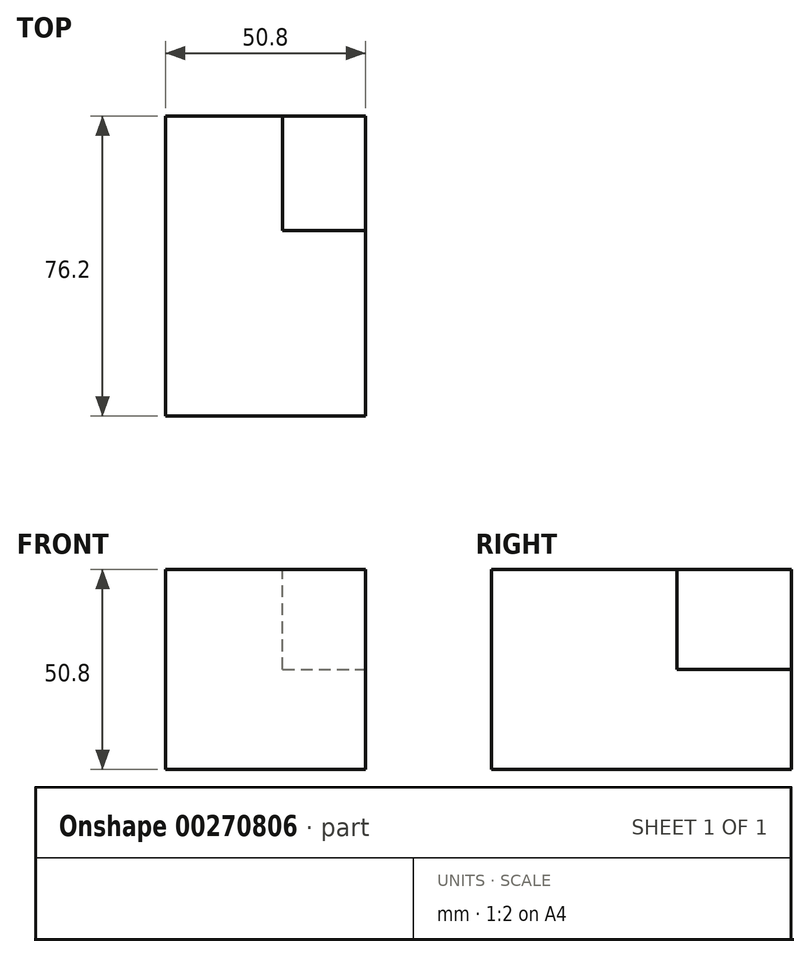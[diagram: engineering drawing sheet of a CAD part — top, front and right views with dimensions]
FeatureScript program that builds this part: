
annotation { "Feature Type Name" : "Feature", "Feature Type Description" : "" }
export const myFeature = defineFeature(function(context is Context, id is Id, definition is map)
    precondition{}
    {
        {
            var Q0;
            Q0=qCreatedBy(makeId("Front.planeOp"),FACE);
            var sketch = newSketch(context, id + "F0", { "sketchPlane" : qUnion([Q0])});
            skLineSegment(sketch, "E0", {"start": v(0, 0) * mm, "end": v(-50.8, 0) * mm});
            skLineSegment(sketch, "E1", {"start": v(-50.8, 0) * mm, "end": v(-50.8, 50.8) * mm});
            skLineSegment(sketch, "E2", {"start": v(-50.8, 50.8) * mm, "end": v(0, 50.8) * mm});
            skLineSegment(sketch, "E3", {"start": v(0, 50.8) * mm, "end": v(0, 0) * mm});
            skSolve(sketch);
        }
        {
            var Q0;
            Q0 = qSketchRegion(id + "F0", true);
            extrude(context, id + "F1", {"entities" : qUnion([Q0]), "depth" : 76.2 * mm});
        }
        {
            var Q0;
            Q0=makeQuery(id+"F1.opExtrude","SWEPT_FACE",FACE,{"disambiguationData":[OSD([sQuery(id+"F0.wireOp",EDGE,"E2")])]});
            var sketch = newSketch(context, id + "F2", { "sketchPlane" : qUnion([Q0])});
            skLineSegment(sketch, "E4", {"start": v(-21.04, 0) * mm, "end": v(-21.04, -29.03) * mm});
            skLineSegment(sketch, "E5", {"start": v(-21.04, -29.03) * mm, "end": v(0, -29.03) * mm});
            skSolve(sketch);
        }
        {
            var Q0;
            {var subQ0=sQuery(id+"F2.wireOp",EDGE,"E4");Q0=makeQuery(id+"F2.imprint","IMPRINT",FACE,{"disambiguationData":[TD([[makeQuery(id+"F2.imprint","IMPRINT",EDGE,{"derivedFrom":subQ0}),1.0]])]});}
            var Q1;
            Q1=sQuery(id+"F2.wireOp",EDGE,"E4");
            var Q2;
            Q2=sQuery(id+"F2.wireOp",EDGE,"E5");
            extrude(context, id + "F3", {"entities" : qUnion([Q0]), "operationType" : NewBodyOperationType.REMOVE, "surfaceEntities" : qUnion([Q1, Q2]), "oppositeDirection" : true, "depth" : 25.4 * mm});
        }
    });
